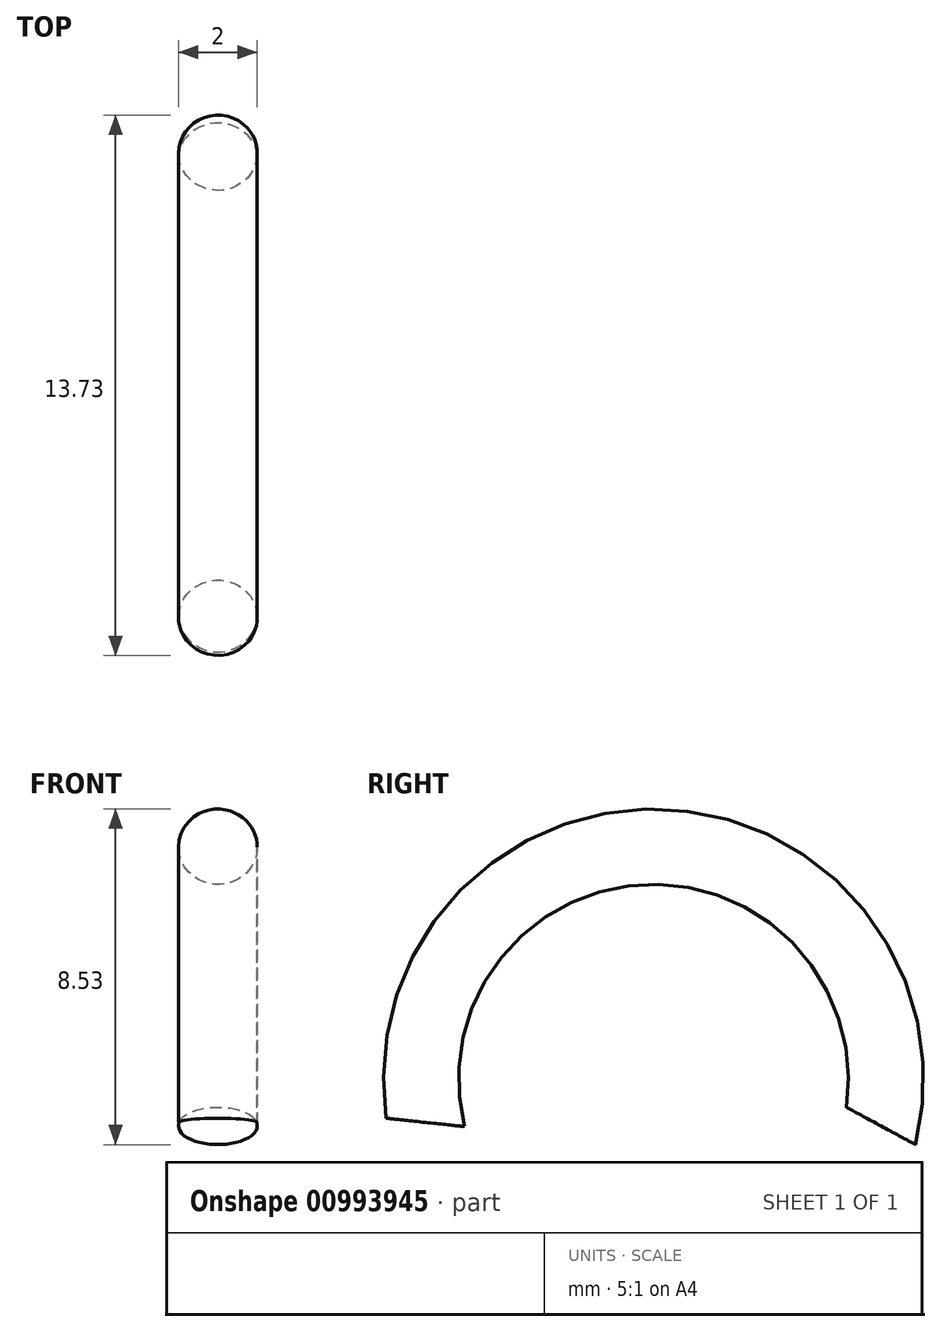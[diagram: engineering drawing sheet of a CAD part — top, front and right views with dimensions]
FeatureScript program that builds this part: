
annotation { "Feature Type Name" : "Feature", "Feature Type Description" : "" }
export const myFeature = defineFeature(function(context is Context, id is Id, definition is map)
    precondition{}
    {
        {
            var Q0;
            Q0=qCreatedBy(makeId("Right.planeOp"),FACE);
            var sketch = newSketch(context, id + "F0", { "sketchPlane" : qUnion([Q0])});
            skArc(sketch, "E0", {"start": v(5.93, -2.82) * mm, "mid": v(0.28, 4.05) * mm, "end": v(-5.36, -2.82) * mm});
            skSolve(sketch);
        }
        {
            var Q0;
            Q0=qCreatedBy(makeId("Top.planeOp"),FACE);
            var sketch = newSketch(context, id + "F1", { "sketchPlane" : qUnion([Q0])});
            skCircle(sketch, "E1", {"center": v(0, 5.93) * mm, "radius": 1 * mm});
            skSolve(sketch);
        }
        {
            var Q0;
            Q0=makeQuery(id+"F1.imprint","IMPRINT",FACE,{"disambiguationData":[TD([[makeQuery(id+"F1.imprint","IMPRINT",EDGE,{"derivedFrom":sQuery(id+"F1.wireOp",EDGE,"E1")}),1.0]])]});
            var Q1;
            Q1=sQuery(id+"F0.wireOp",EDGE,"E0");
            sweep(context, id + "F2", {"profiles" : qUnion([Q0]), "path" : qUnion([Q1])});
        }
    });
